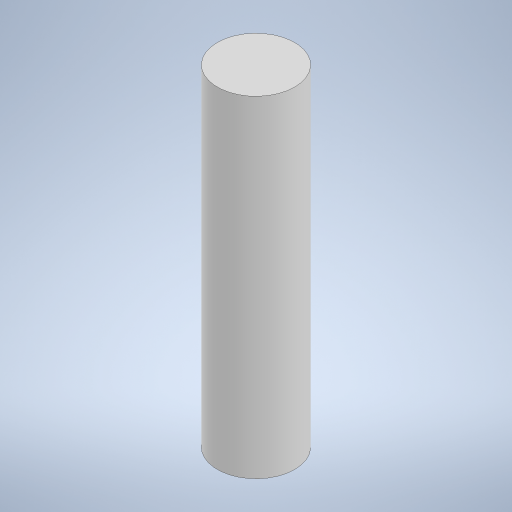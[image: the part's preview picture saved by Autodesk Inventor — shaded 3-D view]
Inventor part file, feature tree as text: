
AUTODESK INVENTOR PART (.ipt)
format: ipt  version: 2024 (Build 280153000, 153)  size: 214,016 bytes
history: native  units: mm
features: other x1, extrude x1, sketch x1
ambient origin geometry x8: Origin, YZ Plane, XZ Plane, XY Plane, X Axis, Y Axis, Z Axis, Center Point
bodies: Body1 (feature_tree)
feature tree (3):
  other  "Твердое тело1"
  extrude  "Выдавливание1"  Depth=3.5mm
  sketch  "Эскиз1"
